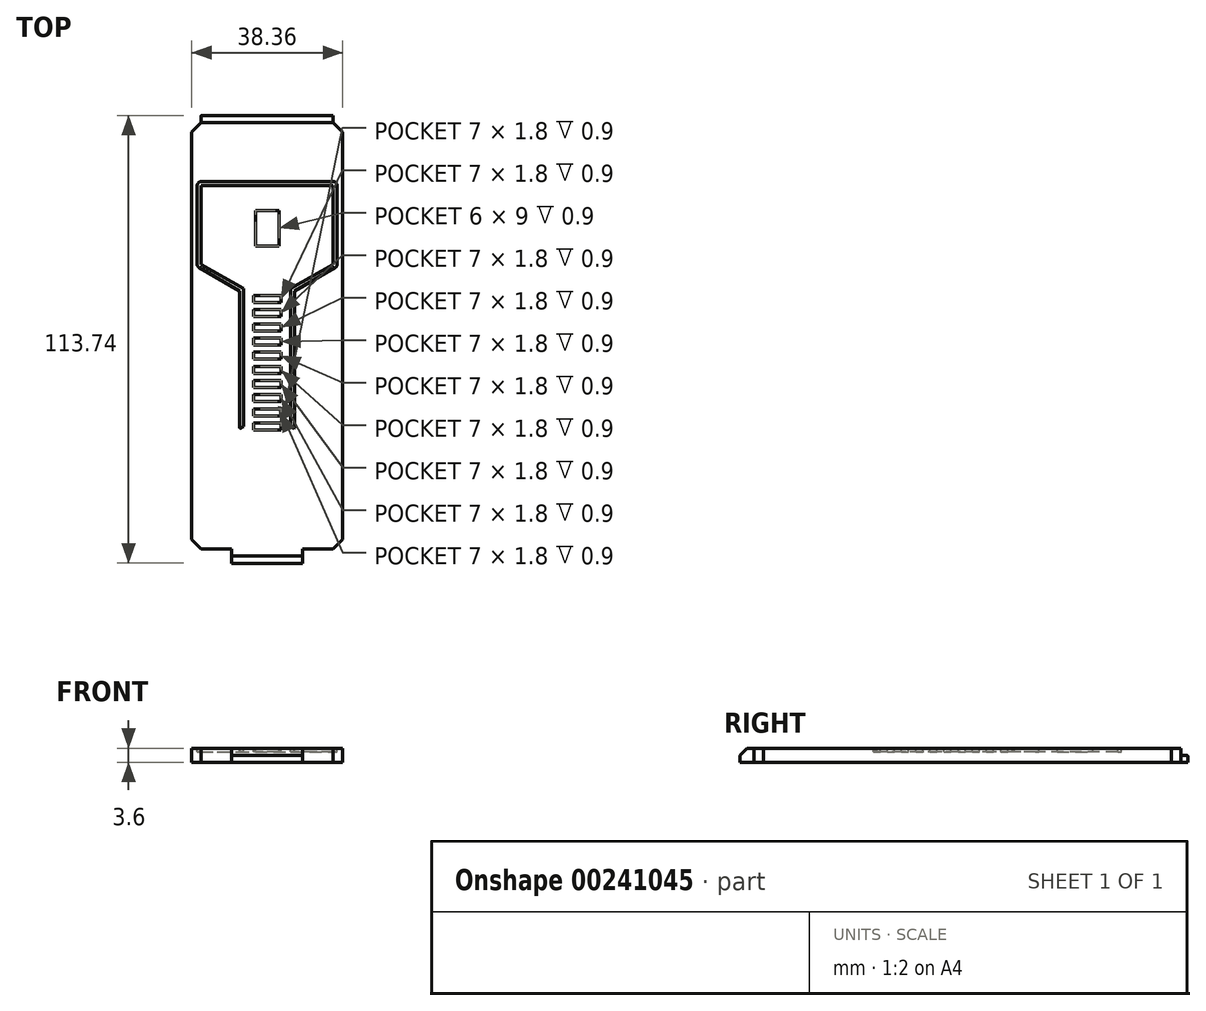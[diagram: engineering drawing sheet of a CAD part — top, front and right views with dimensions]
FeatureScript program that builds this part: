
annotation { "Feature Type Name" : "Feature", "Feature Type Description" : "" }
export const myFeature = defineFeature(function(context is Context, id is Id, definition is map)
    precondition{}
    {
        {
            assignVariable(context, id + "F0", {"name" : "O", "anyValue" : 3.6});
        }
        {
            var Q0;
            Q0=qCreatedBy(makeId("Top.planeOp"),FACE);
            var sketch = newSketch(context, id + "F1", { "sketchPlane" : qUnion([Q0])});
            skLineSegment(sketch, "E0.bottom", {"start": v(19.17, 54.18) * mm, "end": v(-19.18, 54.18) * mm});
            skLineSegment(sketch, "E0.top", {"start": v(19.18, -54.18) * mm, "end": v(-19.17, -54.18) * mm});
            skLineSegment(sketch, "E0.left", {"start": v(19.17, 54.18) * mm, "end": v(19.18, -54.18) * mm});
            skLineSegment(sketch, "E0.right", {"start": v(-19.18, 54.18) * mm, "end": v(-19.17, -54.18) * mm});
            skPoint(sketch, "E0.middle", {"position": v(0, 0) * mm});
            skSolve(sketch);
        }
        {
            var Q0;
            Q0=makeQuery(id+"F1.imprint","IMPRINT",FACE,{"disambiguationData":[TD([[makeQuery(id+"F1.imprint","IMPRINT",EDGE,{"derivedFrom":sQuery(id+"F1.wireOp",EDGE,"E0.bottom")}),1.0]])]});
            extrude(context, id + "F2", {"entities" : qUnion([Q0]), "depth" : (getVariable(context, 'O')) * mm});
        }
        {
            var Q0;
            Q0=makeQuery(id+"F2.opExtrude","SWEPT_EDGE",EDGE,{"disambiguationData":[OSD([sQuery(id+"F1.wireOp",EDGE,"E0.top"),sQuery(id+"F1.wireOp",EDGE,"E0.left")])]});
            var Q1;
            Q1=makeQuery(id+"F2.opExtrude","SWEPT_EDGE",EDGE,{"disambiguationData":[OSD([sQuery(id+"F1.wireOp",EDGE,"E0.top"),sQuery(id+"F1.wireOp",EDGE,"E0.right")])]});
            var Q2;
            Q2=makeQuery(id+"F2.opExtrude","SWEPT_EDGE",EDGE,{"disambiguationData":[OSD([sQuery(id+"F1.wireOp",EDGE,"E0.bottom"),sQuery(id+"F1.wireOp",EDGE,"E0.right")])]});
            var Q3;
            Q3=makeQuery(id+"F2.opExtrude","SWEPT_EDGE",EDGE,{"disambiguationData":[OSD([sQuery(id+"F1.wireOp",EDGE,"E0.bottom"),sQuery(id+"F1.wireOp",EDGE,"E0.left")])]});
            chamfer(context, id + "F3", {"entities" : qUnion([Q0, Q1, Q2, Q3]), "width" : (getVariable(context, 'O') * 0.67) * mm, "tangentPropagation" : true});
        }
        {
            var Q0;
            Q0=makeQuery(id+"F2.opExtrude","SWEPT_FACE",FACE,{"disambiguationData":[OSD([sQuery(id+"F1.wireOp",EDGE,"E0.bottom")])]});
            var sketch = newSketch(context, id + "F4", { "sketchPlane" : qUnion([Q0])});
            skLineSegment(sketch, "E1", {"start": v(-16.78, 1.8) * mm, "end": v(16.78, 1.8) * mm});
            skSolve(sketch);
        }
        {
            var Q0;
            {var subQ0=sQuery(id+"F4.wireOp",EDGE,"E1");Q0=makeQuery(id+"F4.imprint","IMPRINT",FACE,{"disambiguationData":[TD([[makeQuery(id+"F4.imprint","IMPRINT",EDGE,{"derivedFrom":subQ0}),-1.0]])]});}
            extrude(context, id + "F5", {"entities" : qUnion([Q0]), "operationType" : NewBodyOperationType.ADD, "depth" : (getVariable(context, 'O') / 2) * mm});
        }
        {
            var Q0;
            Q0=makeQuery(id+"F5.opExtrude","CAP_EDGE",EDGE,{"disambiguationData":[OSD([sQuery(id+"F4.wireOp",EDGE,"E1")])],"isStart":false});
            fillet(context, id + "F6", {"entities" : qUnion([Q0]), "radius" : .25 * mm, "tangentPropagation" : true, "allowEdgeOverflow" : false});
        }
        {
            var Q0;
            Q0=makeQuery(id+"F2.opExtrude","SWEPT_FACE",FACE,{"disambiguationData":[OSD([sQuery(id+"F1.wireOp",EDGE,"E0.top")])]});
            var sketch = newSketch(context, id + "F7", { "sketchPlane" : qUnion([Q0])});
            skLineSegment(sketch, "E2.bottom", {"start": v(9, 0) * mm, "end": v(-9, 0) * mm});
            skLineSegment(sketch, "E2.top", {"start": v(9, 3.6) * mm, "end": v(-9, 3.6) * mm});
            skLineSegment(sketch, "E2.left", {"start": v(9, 0) * mm, "end": v(9, 3.6) * mm});
            skLineSegment(sketch, "E2.right", {"start": v(-9, 0) * mm, "end": v(-9, 3.6) * mm});
            skPoint(sketch, "E2.middle", {"position": v(0, 1.8) * mm});
            skPoint(sketch, "E2.middle.positionSnap0", {"position": v(-16.78, 1.8) * mm});
            skPoint(sketch, "E2.centerSnap0", {"position": v(-16.78, 1.8) * mm});
            skSolve(sketch);
        }
        {
            var Q0;
            Q0=makeQuery(id+"F7.imprint","IMPRINT",FACE,{"disambiguationData":[TD([[makeQuery(id+"F7.imprint","IMPRINT",EDGE,{"derivedFrom":sQuery(id+"F7.wireOp",EDGE,"E2.bottom")}),-1.0]])]});
            extrude(context, id + "F8", {"entities" : qUnion([Q0]), "operationType" : NewBodyOperationType.ADD, "depth" : (getVariable(context, 'O')) * mm});
        }
        {
            var Q0;
            Q0=makeQuery(id+"F8.opExtrude","CAP_EDGE",EDGE,{"disambiguationData":[OSD([sQuery(id+"F7.wireOp",EDGE,"E2.top")])],"isStart":false});
            chamfer(context, id + "F9", {"entities" : qUnion([Q0]), "width" : (getVariable(context, 'O') / 2) * mm, "tangentPropagation" : true});
        }
        {
            var Q0;
            Q0=makeQuery(id+"F8.boolean.opBoolean","MERGE",FACE,{"derivedFrom":[makeQuery(id+"F2.opExtrude","CAP_FACE",FACE,{"disambiguationData":[OSD([sQuery(id+"F1.wireOp",EDGE,"E0.bottom"),sQuery(id+"F1.wireOp",EDGE,"E0.top"),sQuery(id+"F1.wireOp",EDGE,"E0.left"),sQuery(id+"F1.wireOp",EDGE,"E0.right")])],"isStart":false}),makeQuery(id+"F8.opExtrude","SWEPT_FACE",FACE,{"disambiguationData":[OSD([sQuery(id+"F7.wireOp",EDGE,"E2.top")])]})]});
            var sketch = newSketch(context, id + "F10", { "sketchPlane" : qUnion([Q0])});
            skLineSegment(sketch, "E3", {"start": v(-16.78, 38.17) * mm, "end": v(16.78, 38.18) * mm});
            skLineSegment(sketch, "E4", {"start": v(16.78, 38.18) * mm, "end": v(16.78, 18.18) * mm});
            skLineSegment(sketch, "E5", {"start": v(16.78, 18.18) * mm, "end": v(6, 11.95) * mm});
            skLineSegment(sketch, "E6", {"start": v(6, 11.95) * mm, "end": v(6, -23.05) * mm});
            skLineSegment(sketch, "E7", {"start": v(6, -23.05) * mm, "end": v(19.18, -30.65) * mm});
            skLineSegment(sketch, "E8", {"start": v(-16.78, 38.17) * mm, "end": v(-16.78, 18.18) * mm});
            skLineSegment(sketch, "E9", {"start": v(-16.78, 18.18) * mm, "end": v(-6, 11.95) * mm});
            skLineSegment(sketch, "E10", {"start": v(-6, 11.95) * mm, "end": v(-6, -23.05) * mm});
            skLineSegment(sketch, "E11", {"start": v(-6, -23.05) * mm, "end": v(-19.17, -30.65) * mm});
            skArc(sketch, "E12.0.startCap", {"start": v(-7, 11.95) * mm, "mid": v(-6, 12.95) * mm, "end": v(-5, 11.95) * mm});
            skArc(sketch, "E12.0.endCap", {"start": v(-5, -23.05) * mm, "mid": v(-6, -24.05) * mm, "end": v(-7, -23.05) * mm});
            skLineSegment(sketch, "E12.0.left", {"start": v(-5, 11.95) * mm, "end": v(-5, -23.05) * mm});
            skLineSegment(sketch, "E12.0.right", {"start": v(-7, 11.95) * mm, "end": v(-7, -23.05) * mm});
            skArc(sketch, "E12.1.startCap", {"start": v(-17.28, 17.3) * mm, "mid": v(-17.64, 18.68) * mm, "end": v(-16.28, 19.04) * mm});
            skArc(sketch, "E12.1.endCap", {"start": v(-5.5, 12.82) * mm, "mid": v(-5.13, 11.45) * mm, "end": v(-6.5, 11.09) * mm});
            skLineSegment(sketch, "E12.1.left", {"start": v(-16.28, 19.04) * mm, "end": v(-5.5, 12.82) * mm});
            skLineSegment(sketch, "E12.1.right", {"start": v(-17.28, 17.3) * mm, "end": v(-6.5, 11.09) * mm});
            skArc(sketch, "E12.2.startCap", {"start": v(-17.78, 38.17) * mm, "mid": v(-16.78, 39.18) * mm, "end": v(-15.78, 38.17) * mm});
            skArc(sketch, "E12.2.endCap", {"start": v(-15.78, 18.18) * mm, "mid": v(-16.78, 17.18) * mm, "end": v(-17.78, 18.18) * mm});
            skLineSegment(sketch, "E12.2.left", {"start": v(-15.78, 38.17) * mm, "end": v(-15.78, 18.18) * mm});
            skLineSegment(sketch, "E12.2.right", {"start": v(-17.78, 38.17) * mm, "end": v(-17.78, 18.18) * mm});
            skArc(sketch, "E12.3.startCap", {"start": v(-16.78, 37.17) * mm, "mid": v(-17.78, 38.17) * mm, "end": v(-16.78, 39.18) * mm});
            skArc(sketch, "E12.3.endCap", {"start": v(16.78, 39.18) * mm, "mid": v(17.78, 38.18) * mm, "end": v(16.78, 37.18) * mm});
            skLineSegment(sketch, "E12.3.left", {"start": v(-16.78, 39.18) * mm, "end": v(16.78, 39.18) * mm});
            skLineSegment(sketch, "E12.3.right", {"start": v(-16.78, 37.17) * mm, "end": v(16.78, 37.18) * mm});
            skArc(sketch, "E12.4.startCap", {"start": v(15.78, 38.18) * mm, "mid": v(16.78, 39.18) * mm, "end": v(17.78, 38.18) * mm});
            skArc(sketch, "E12.4.endCap", {"start": v(17.78, 18.18) * mm, "mid": v(16.78, 17.18) * mm, "end": v(15.78, 18.18) * mm});
            skLineSegment(sketch, "E12.4.left", {"start": v(17.78, 38.18) * mm, "end": v(17.78, 18.18) * mm});
            skLineSegment(sketch, "E12.4.right", {"start": v(15.78, 38.18) * mm, "end": v(15.78, 18.18) * mm});
            skArc(sketch, "E12.5.startCap", {"start": v(16.28, 19.04) * mm, "mid": v(17.64, 18.68) * mm, "end": v(17.28, 17.3) * mm});
            skArc(sketch, "E12.5.endCap", {"start": v(6.5, 11.09) * mm, "mid": v(5.13, 11.45) * mm, "end": v(5.5, 12.82) * mm});
            skLineSegment(sketch, "E12.5.left", {"start": v(17.28, 17.3) * mm, "end": v(6.5, 11.09) * mm});
            skLineSegment(sketch, "E12.5.right", {"start": v(16.28, 19.04) * mm, "end": v(5.5, 12.82) * mm});
            skArc(sketch, "E12.6.startCap", {"start": v(5, 11.95) * mm, "mid": v(6, 12.95) * mm, "end": v(7, 11.95) * mm});
            skArc(sketch, "E12.6.endCap", {"start": v(7, -23.05) * mm, "mid": v(6, -24.05) * mm, "end": v(5, -23.05) * mm});
            skLineSegment(sketch, "E12.6.left", {"start": v(7, 11.95) * mm, "end": v(7, -23.05) * mm});
            skLineSegment(sketch, "E12.6.right", {"start": v(5, 11.95) * mm, "end": v(5, -23.05) * mm});
            skArc(sketch, "E13.0.startCap", {"start": v(-6.5, -22.18) * mm, "mid": v(-5.13, -22.55) * mm, "end": v(-5.5, -23.91) * mm});
            skArc(sketch, "E13.0.endCap", {"start": v(-18.67, -31.52) * mm, "mid": v(-20.04, -31.15) * mm, "end": v(-19.67, -29.79) * mm});
            skLineSegment(sketch, "E13.0.left", {"start": v(-5.5, -23.91) * mm, "end": v(-18.67, -31.52) * mm});
            skLineSegment(sketch, "E13.0.right", {"start": v(-6.5, -22.18) * mm, "end": v(-19.67, -29.79) * mm});
            skArc(sketch, "E13.1.startCap", {"start": v(5.5, -23.91) * mm, "mid": v(5.13, -22.55) * mm, "end": v(6.5, -22.18) * mm});
            skArc(sketch, "E13.1.endCap", {"start": v(19.67, -29.79) * mm, "mid": v(20.04, -31.15) * mm, "end": v(18.67, -31.52) * mm});
            skLineSegment(sketch, "E13.1.left", {"start": v(6.5, -22.18) * mm, "end": v(19.67, -29.79) * mm});
            skLineSegment(sketch, "E13.1.right", {"start": v(5.5, -23.91) * mm, "end": v(18.68, -31.52) * mm});
            skLineSegment(sketch, "E14.bottom", {"start": v(3, 22.83) * mm, "end": v(-3, 22.83) * mm});
            skLineSegment(sketch, "E14.top", {"start": v(3, 31.83) * mm, "end": v(-3, 31.83) * mm});
            skLineSegment(sketch, "E14.left", {"start": v(3, 22.83) * mm, "end": v(3, 31.83) * mm});
            skLineSegment(sketch, "E14.right", {"start": v(-3, 22.83) * mm, "end": v(-3, 31.83) * mm});
            skPoint(sketch, "E14.middle", {"position": v(0, 27.33) * mm});
            skLineSegment(sketch, "E15.bottom", {"start": v(3.5, -23.95) * mm, "end": v(-3.5, -23.95) * mm});
            skLineSegment(sketch, "E15.top", {"start": v(3.5, -22.15) * mm, "end": v(-3.5, -22.15) * mm});
            skLineSegment(sketch, "E15.left", {"start": v(3.5, -23.95) * mm, "end": v(3.5, -22.15) * mm});
            skLineSegment(sketch, "E15.right", {"start": v(-3.5, -23.95) * mm, "end": v(-3.5, -22.15) * mm});
            skPoint(sketch, "E15.middle", {"position": v(0, -23.05) * mm});
            skLineSegment(sketch, "E16.0.1.0", {"start": v(3.5, -18.55) * mm, "end": v(-3.5, -18.55) * mm});
            skLineSegment(sketch, "E16.0.1.1", {"start": v(-3.5, -20.35) * mm, "end": v(-3.5, -18.55) * mm});
            skLineSegment(sketch, "E16.0.1.2", {"start": v(3.5, -20.35) * mm, "end": v(-3.5, -20.35) * mm});
            skLineSegment(sketch, "E16.0.1.3", {"start": v(3.5, -20.35) * mm, "end": v(3.5, -18.55) * mm});
            skLineSegment(sketch, "E16.0.2.0", {"start": v(3.5, -14.95) * mm, "end": v(-3.5, -14.95) * mm});
            skLineSegment(sketch, "E16.0.2.1", {"start": v(-3.5, -16.75) * mm, "end": v(-3.5, -14.95) * mm});
            skLineSegment(sketch, "E16.0.2.2", {"start": v(3.5, -16.75) * mm, "end": v(-3.5, -16.75) * mm});
            skLineSegment(sketch, "E16.0.2.3", {"start": v(3.5, -16.75) * mm, "end": v(3.5, -14.95) * mm});
            skLineSegment(sketch, "E16.0.3.0", {"start": v(3.5, -11.35) * mm, "end": v(-3.5, -11.35) * mm});
            skLineSegment(sketch, "E16.0.3.1", {"start": v(-3.5, -13.15) * mm, "end": v(-3.5, -11.35) * mm});
            skLineSegment(sketch, "E16.0.3.2", {"start": v(3.5, -13.15) * mm, "end": v(-3.5, -13.15) * mm});
            skLineSegment(sketch, "E16.0.3.3", {"start": v(3.5, -13.15) * mm, "end": v(3.5, -11.35) * mm});
            skLineSegment(sketch, "E16.0.4.0", {"start": v(3.5, -7.75) * mm, "end": v(-3.5, -7.75) * mm});
            skLineSegment(sketch, "E16.0.4.1", {"start": v(-3.5, -9.55) * mm, "end": v(-3.5, -7.75) * mm});
            skLineSegment(sketch, "E16.0.4.2", {"start": v(3.5, -9.55) * mm, "end": v(-3.5, -9.55) * mm});
            skLineSegment(sketch, "E16.0.4.3", {"start": v(3.5, -9.55) * mm, "end": v(3.5, -7.75) * mm});
            skLineSegment(sketch, "E16.0.5.0", {"start": v(3.5, -4.15) * mm, "end": v(-3.5, -4.15) * mm});
            skLineSegment(sketch, "E16.0.5.1", {"start": v(-3.5, -5.95) * mm, "end": v(-3.5, -4.15) * mm});
            skLineSegment(sketch, "E16.0.5.2", {"start": v(3.5, -5.95) * mm, "end": v(-3.5, -5.95) * mm});
            skLineSegment(sketch, "E16.0.5.3", {"start": v(3.5, -5.95) * mm, "end": v(3.5, -4.15) * mm});
            skLineSegment(sketch, "E16.0.6.0", {"start": v(3.5, -0.55) * mm, "end": v(-3.5, -0.55) * mm});
            skLineSegment(sketch, "E16.0.6.1", {"start": v(-3.5, -2.35) * mm, "end": v(-3.5, -0.55) * mm});
            skLineSegment(sketch, "E16.0.6.2", {"start": v(3.5, -2.35) * mm, "end": v(-3.5, -2.35) * mm});
            skLineSegment(sketch, "E16.0.6.3", {"start": v(3.5, -2.35) * mm, "end": v(3.5, -0.55) * mm});
            skLineSegment(sketch, "E16.0.7.0", {"start": v(3.5, 3.05) * mm, "end": v(-3.5, 3.05) * mm});
            skLineSegment(sketch, "E16.0.7.1", {"start": v(-3.5, 1.25) * mm, "end": v(-3.5, 3.05) * mm});
            skLineSegment(sketch, "E16.0.7.2", {"start": v(3.5, 1.25) * mm, "end": v(-3.5, 1.25) * mm});
            skLineSegment(sketch, "E16.0.7.3", {"start": v(3.5, 1.25) * mm, "end": v(3.5, 3.05) * mm});
            skLineSegment(sketch, "E16.0.8.0", {"start": v(3.5, 6.65) * mm, "end": v(-3.5, 6.65) * mm});
            skLineSegment(sketch, "E16.0.8.1", {"start": v(-3.5, 4.85) * mm, "end": v(-3.5, 6.65) * mm});
            skLineSegment(sketch, "E16.0.8.2", {"start": v(3.5, 4.85) * mm, "end": v(-3.5, 4.85) * mm});
            skLineSegment(sketch, "E16.0.8.3", {"start": v(3.5, 4.85) * mm, "end": v(3.5, 6.65) * mm});
            skLineSegment(sketch, "E16.0.9.0", {"start": v(3.5, 10.25) * mm, "end": v(-3.5, 10.25) * mm});
            skLineSegment(sketch, "E16.0.9.1", {"start": v(-3.5, 8.45) * mm, "end": v(-3.5, 10.25) * mm});
            skLineSegment(sketch, "E16.0.9.2", {"start": v(3.5, 8.45) * mm, "end": v(-3.5, 8.45) * mm});
            skLineSegment(sketch, "E16.0.9.3", {"start": v(3.5, 8.45) * mm, "end": v(3.5, 10.25) * mm});
            skLineSegment(sketch, "E16.direction1", {"start": v(-3.5, -22.15) * mm, "end": v(21.5, -22.15) * mm, "construction": true});
            skLineSegment(sketch, "E16.direction2", {"start": v(-3.5, -22.15) * mm, "end": v(-3.5, -18.55) * mm, "construction": true});
            skSolve(sketch);
        }
        {
            var Q0;
            Q0=makeQuery(id+"F10.imprint","IMPRINT",FACE,{"disambiguationData":[TD([[makeQuery(id+"F10.imprint","IMPRINT",EDGE,{"derivedFrom":sQuery(id+"F10.wireOp",EDGE,"E15.bottom")}),-1.0]])]});
            var Q1;
            Q1=makeQuery(id+"F10.imprint","IMPRINT",FACE,{"disambiguationData":[TD([[makeQuery(id+"F10.imprint","IMPRINT",EDGE,{"derivedFrom":sQuery(id+"F10.wireOp",EDGE,"E16.0.1.0")}),1.0]])]});
            var Q2;
            Q2=makeQuery(id+"F10.imprint","IMPRINT",FACE,{"disambiguationData":[TD([[makeQuery(id+"F10.imprint","IMPRINT",EDGE,{"derivedFrom":sQuery(id+"F10.wireOp",EDGE,"E16.0.2.0")}),1.0]])]});
            var Q3;
            Q3=makeQuery(id+"F10.imprint","IMPRINT",FACE,{"disambiguationData":[TD([[makeQuery(id+"F10.imprint","IMPRINT",EDGE,{"derivedFrom":sQuery(id+"F10.wireOp",EDGE,"E16.0.3.0")}),1.0]])]});
            var Q4;
            Q4=makeQuery(id+"F10.imprint","IMPRINT",FACE,{"disambiguationData":[TD([[makeQuery(id+"F10.imprint","IMPRINT",EDGE,{"derivedFrom":sQuery(id+"F10.wireOp",EDGE,"E16.0.4.0")}),1.0]])]});
            var Q5;
            Q5=makeQuery(id+"F10.imprint","IMPRINT",FACE,{"disambiguationData":[TD([[makeQuery(id+"F10.imprint","IMPRINT",EDGE,{"derivedFrom":sQuery(id+"F10.wireOp",EDGE,"E16.0.5.0")}),1.0]])]});
            var Q6;
            Q6=makeQuery(id+"F10.imprint","IMPRINT",FACE,{"disambiguationData":[TD([[makeQuery(id+"F10.imprint","IMPRINT",EDGE,{"derivedFrom":sQuery(id+"F10.wireOp",EDGE,"E16.0.6.0")}),1.0]])]});
            var Q7;
            Q7=makeQuery(id+"F10.imprint","IMPRINT",FACE,{"disambiguationData":[TD([[makeQuery(id+"F10.imprint","IMPRINT",EDGE,{"derivedFrom":sQuery(id+"F10.wireOp",EDGE,"E16.0.7.0")}),1.0]])]});
            var Q8;
            Q8=makeQuery(id+"F10.imprint","IMPRINT",FACE,{"disambiguationData":[TD([[makeQuery(id+"F10.imprint","IMPRINT",EDGE,{"derivedFrom":sQuery(id+"F10.wireOp",EDGE,"E16.0.8.0")}),1.0]])]});
            var Q9;
            Q9=makeQuery(id+"F10.imprint","IMPRINT",FACE,{"disambiguationData":[TD([[makeQuery(id+"F10.imprint","IMPRINT",EDGE,{"derivedFrom":sQuery(id+"F10.wireOp",EDGE,"E16.0.9.0")}),1.0]])]});
            var Q10;
            Q10=makeQuery(id+"F10.imprint","IMPRINT",FACE,{"disambiguationData":[TD([[makeQuery(id+"F10.imprint","IMPRINT",EDGE,{"derivedFrom":sQuery(id+"F10.wireOp",EDGE,"E14.bottom")}),-1.0]])]});
            var Q11;
            {var subQ1=sQuery(id+"F10.wireOp",EDGE,"E12.1.endCap");var subQ5=sQuery(id+"F10.wireOp",EDGE,"E10");var subQ6=makeQuery(id+"F10.imprint","INTERSECT",VERTEX,{"derivedFrom":[subQ5,subQ1]});Q11=makeQuery(id+"F10.imprint","IMPRINT",FACE,{"disambiguationData":[TD([[makeQuery(id+"F10.imprint","IMPRINT",EDGE,{"disambiguationData":[TD([[subQ6,-1.0]])],"derivedFrom":subQ5}),-1.0]])]});}
            var Q12;
            {var subQ5=sQuery(id+"F10.wireOp",EDGE,"E11");var subQ6=sQuery(id+"F10.wireOp",EDGE,"E10");var subQ7=makeQuery(id+"F10.imprint","INTERSECT",VERTEX,{"derivedFrom":[subQ6,subQ5]});Q12=makeQuery(id+"F10.imprint","IMPRINT",FACE,{"disambiguationData":[TD([[makeQuery(id+"F10.imprint","IMPRINT",EDGE,{"disambiguationData":[TD([[subQ7,1.0]])],"derivedFrom":subQ6}),-1.0]])]});}
            var Q13;
            {var subQ5=sQuery(id+"F10.wireOp",EDGE,"E7");var subQ7=sQuery(id+"F10.wireOp",EDGE,"E6");var subQ8=makeQuery(id+"F10.imprint","INTERSECT",VERTEX,{"derivedFrom":[subQ7,subQ5]});Q13=makeQuery(id+"F10.imprint","IMPRINT",FACE,{"disambiguationData":[TD([[makeQuery(id+"F10.imprint","IMPRINT",EDGE,{"disambiguationData":[TD([[subQ8,1.0]])],"derivedFrom":subQ7}),1.0]])]});}
            var Q14;
            {var subQ5=sQuery(id+"F10.wireOp",EDGE,"E12.5.endCap");var subQ7=sQuery(id+"F10.wireOp",EDGE,"E6");var subQ8=makeQuery(id+"F10.imprint","INTERSECT",VERTEX,{"derivedFrom":[subQ7,subQ5]});Q14=makeQuery(id+"F10.imprint","IMPRINT",FACE,{"disambiguationData":[TD([[makeQuery(id+"F10.imprint","IMPRINT",EDGE,{"disambiguationData":[TD([[subQ8,-1.0]])],"derivedFrom":subQ7}),1.0]])]});}
            var Q15;
            {var subQ5=sQuery(id+"F10.wireOp",EDGE,"E10");var subQ6=sQuery(id+"F10.wireOp",EDGE,"E9");var subQ7=makeQuery(id+"F10.imprint","INTERSECT",VERTEX,{"derivedFrom":[subQ6,subQ5]});Q15=makeQuery(id+"F10.imprint","IMPRINT",FACE,{"disambiguationData":[TD([[makeQuery(id+"F10.imprint","IMPRINT",EDGE,{"disambiguationData":[TD([[subQ7,1.0]])],"derivedFrom":subQ6}),-1.0]])]});}
            var Q16;
            {var subQ0=sQuery(id+"F10.wireOp",EDGE,"E12.2.endCap");var subQ7=sQuery(id+"F10.wireOp",EDGE,"E9");var subQ9=makeQuery(id+"F10.imprint","INTERSECT",VERTEX,{"derivedFrom":[subQ7,subQ0]});Q16=makeQuery(id+"F10.imprint","IMPRINT",FACE,{"disambiguationData":[TD([[makeQuery(id+"F10.imprint","IMPRINT",EDGE,{"disambiguationData":[TD([[subQ9,-1.0]])],"derivedFrom":subQ7}),-1.0]])]});}
            var Q17;
            {var subQ3=sQuery(id+"F10.wireOp",EDGE,"E8");var subQ6=sQuery(id+"F10.wireOp",EDGE,"E9");var subQ8=makeQuery(id+"F10.imprint","INTERSECT",VERTEX,{"derivedFrom":[subQ3,subQ6]});Q17=makeQuery(id+"F10.imprint","IMPRINT",FACE,{"disambiguationData":[TD([[makeQuery(id+"F10.imprint","IMPRINT",EDGE,{"disambiguationData":[TD([[subQ8,1.0]])],"derivedFrom":subQ3}),-1.0]])]});}
            var Q18;
            {var subQ7=sQuery(id+"F10.wireOp",EDGE,"E5");var subQ9=sQuery(id+"F10.wireOp",EDGE,"E6");var subQ11=makeQuery(id+"F10.imprint","INTERSECT",VERTEX,{"derivedFrom":[subQ7,subQ9]});Q18=makeQuery(id+"F10.imprint","IMPRINT",FACE,{"disambiguationData":[TD([[makeQuery(id+"F10.imprint","IMPRINT",EDGE,{"disambiguationData":[TD([[subQ11,1.0]])],"derivedFrom":subQ7}),1.0]])]});}
            var Q19;
            {var subQ3=sQuery(id+"F10.wireOp",EDGE,"E5");var subQ6=sQuery(id+"F10.wireOp",EDGE,"E12.4.endCap");var subQ8=makeQuery(id+"F10.imprint","INTERSECT",VERTEX,{"derivedFrom":[subQ3,subQ6]});Q19=makeQuery(id+"F10.imprint","IMPRINT",FACE,{"disambiguationData":[TD([[makeQuery(id+"F10.imprint","IMPRINT",EDGE,{"disambiguationData":[TD([[subQ8,-1.0]])],"derivedFrom":subQ3}),1.0]])]});}
            var Q20;
            {var subQ2=sQuery(id+"F10.wireOp",EDGE,"E4");var subQ6=sQuery(id+"F10.wireOp",EDGE,"E5");var subQ8=makeQuery(id+"F10.imprint","INTERSECT",VERTEX,{"derivedFrom":[subQ2,subQ6]});Q20=makeQuery(id+"F10.imprint","IMPRINT",FACE,{"disambiguationData":[TD([[makeQuery(id+"F10.imprint","IMPRINT",EDGE,{"disambiguationData":[TD([[subQ8,1.0]])],"derivedFrom":subQ2}),1.0]])]});}
            var Q21;
            {var subQ0=sQuery(id+"F10.wireOp",EDGE,"E12.3.endCap");Q21=makeQuery(id+"F10.imprint","IMPRINT",FACE,{"disambiguationData":[TD([[makeQuery(id+"F10.imprint","IMPRINT",EDGE,{"derivedFrom":subQ0}),1.0]])]});}
            var Q22;
            {var subQ5=sQuery(id+"F10.wireOp",EDGE,"E12.2.right");Q22=makeQuery(id+"F10.imprint","IMPRINT",FACE,{"disambiguationData":[TD([[makeQuery(id+"F10.imprint","IMPRINT",EDGE,{"derivedFrom":subQ5}),1.0]])]});}
            var Q23;
            {var subQ4=sQuery(id+"F10.wireOp",EDGE,"E12.2.startCap");Q23=makeQuery(id+"F10.imprint","IMPRINT",FACE,{"disambiguationData":[TD([[makeQuery(id+"F10.imprint","IMPRINT",EDGE,{"derivedFrom":subQ4}),-1.0]])]});}
            var Q24;
            {var subQ4=sQuery(id+"F10.wireOp",EDGE,"E12.3.endCap");Q24=makeQuery(id+"F10.imprint","IMPRINT",FACE,{"disambiguationData":[TD([[makeQuery(id+"F10.imprint","IMPRINT",EDGE,{"derivedFrom":subQ4}),-1.0]])]});}
            var Q25;
            {var subQ0=sQuery(id+"F10.wireOp",EDGE,"E12.2.startCap");Q25=makeQuery(id+"F10.imprint","IMPRINT",FACE,{"disambiguationData":[TD([[makeQuery(id+"F10.imprint","IMPRINT",EDGE,{"derivedFrom":subQ0}),1.0]])]});}
            extrude(context, id + "F11", {"entities" : qUnion([Q0, Q1, Q2, Q3, Q4, Q5, Q6, Q7, Q8, Q9, Q10, Q11, Q12, Q13, Q14, Q15, Q16, Q17, Q18, Q19, Q20, Q21, Q22, Q23, Q24, Q25]), "operationType" : NewBodyOperationType.REMOVE, "oppositeDirection" : true, "depth" : .9 * mm});
        }
    });
